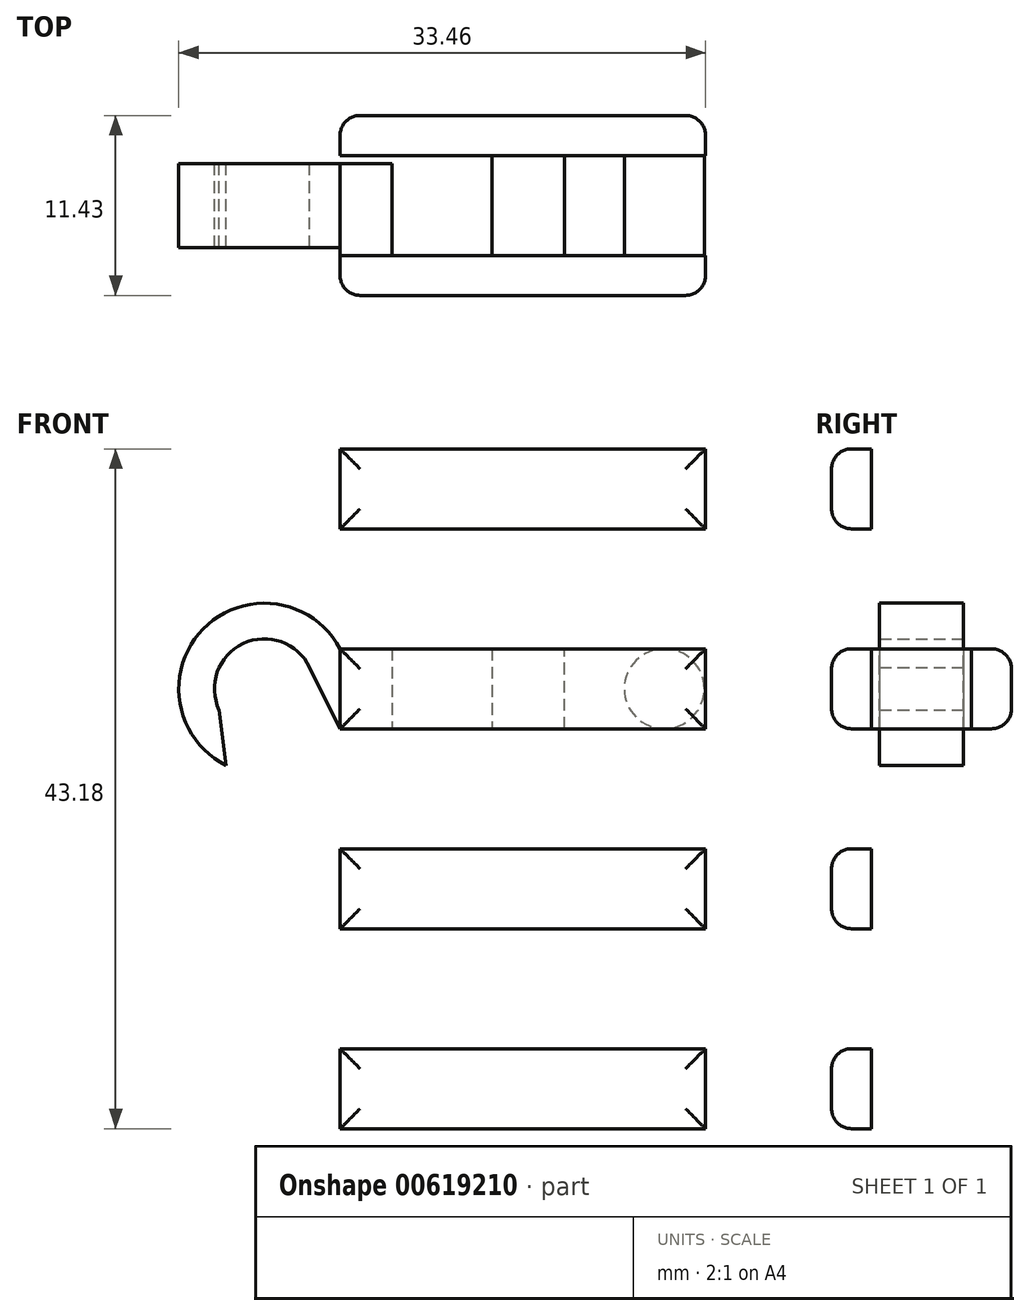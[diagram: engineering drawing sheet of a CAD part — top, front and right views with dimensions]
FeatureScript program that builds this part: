
annotation { "Feature Type Name" : "Feature", "Feature Type Description" : "" }
export const myFeature = defineFeature(function(context is Context, id is Id, definition is map)
    precondition{}
    {
        {
            var Q0;
            Q0=qCreatedBy(makeId("Front.planeOp"),FACE);
            var sketch = newSketch(context, id + "F0", { "sketchPlane" : qUnion([Q0])});
            skLineSegment(sketch, "E0.bottom", {"start": v(0, 0) * mm, "end": v(12.7, 0) * mm});
            skLineSegment(sketch, "E0.top", {"start": v(0, 5.08) * mm, "end": v(12.7, 5.08) * mm});
            skLineSegment(sketch, "E0.right", {"start": v(12.7, 0) * mm, "end": v(12.7, 5.08) * mm});
            skPoint(sketch, "E1.endSnap0", {"position": v(12.7, 2.54) * mm});
            skCircle(sketch, "E2", {"center": v(19.05, 2.54) * mm, "radius": 2.54 * mm});
            skPoint(sketch, "E3.endSnap0", {"position": v(0, 2.54) * mm});
            skArc(sketch, "E4", {"start": v(-3.48, 3.9) * mm, "mid": v(-7.71, 5.4) * mm, "end": v(-9.22, 1.18) * mm});
            skLineSegment(sketch, "E5", {"start": v(0, 5.08) * mm, "end": v(-1.54, 5.08) * mm});
            skLineSegment(sketch, "E6", {"start": v(-1.54, 0) * mm, "end": v(0, 0) * mm});
            skPoint(sketch, "E7.orphan", {"position": v(-3.18, 2.54) * mm});
            skLineSegment(sketch, "E8", {"start": v(-1.54, 0) * mm, "end": v(-3.48, 3.9) * mm});
            skLineSegment(sketch, "E9", {"start": v(-9.22, 1.18) * mm, "end": v(-8.78, -2.32) * mm});
            skLineSegment(sketch, "E10.trimOffspring", {"start": v(-2.8, 2.54) * mm, "end": v(-2.85, 2.54) * mm});
            skArc(sketch, "E11.trimOffspring", {"start": v(-1.54, 5.08) * mm, "mid": v(-10.24, 6.34) * mm, "end": v(-8.78, -2.32) * mm});
            skPoint(sketch, "E3.start.orphan", {"position": v(0, 2.54) * mm});
            skSolve(sketch);
        }
        {
            var Q0;
            Q0 = qSketchRegion(id + "F0", true);
            extrude(context, id + "F1", {"entities" : qUnion([Q0]), "depth" : 6.35 * mm, "offsetDistance" : 25.4 * mm});
        }
        {
            var Q0;
            Q0=makeQuery(id+"F1.opExtrude","CAP_FACE",FACE,{"disambiguationData":[OSD([sQuery(id+"F0.wireOp",EDGE,"E0.bottom"),sQuery(id+"F0.wireOp",EDGE,"E0.top"),sQuery(id+"F0.wireOp",EDGE,"E0.right"),sQuery(id+"F0.wireOp",EDGE,"E4"),sQuery(id+"F0.wireOp",EDGE,"E5"),sQuery(id+"F0.wireOp",EDGE,"E6"),sQuery(id+"F0.wireOp",EDGE,"E8"),sQuery(id+"F0.wireOp",EDGE,"E9"),sQuery(id+"F0.wireOp",EDGE,"E11.trimOffspring")])],"isStart":false});
            var sketch = newSketch(context, id + "F2", { "sketchPlane" : qUnion([Q0])});
            skLineSegment(sketch, "E12.right", {"start": v(21.67, 5.08) * mm, "end": v(21.67, 0) * mm});
            skLineSegment(sketch, "E13.left", {"start": v(21.67, 0) * mm, "end": v(21.67, 5.08) * mm});
            skLineSegment(sketch, "E14.trimOffspring", {"start": v(10.28, 0) * mm, "end": v(12.7, 0) * mm});
            skLineSegment(sketch, "E15.right", {"start": v(-1.54, 5.08) * mm, "end": v(-1.54, 0) * mm});
            skPoint(sketch, "E16.top.end.orphan", {"position": v(2.54, 0) * mm});
            skLineSegment(sketch, "E17", {"start": v(12.7, 0) * mm, "end": v(21.67, 0) * mm});
            skLineSegment(sketch, "E18", {"start": v(21.67, 5.08) * mm, "end": v(-1.54, 5.08) * mm});
            skLineSegment(sketch, "E19", {"start": v(-1.54, 0) * mm, "end": v(21.67, 0) * mm});
            skSolve(sketch);
        }
        {
            var Q0;
            Q0 = qSketchRegion(id + "F2", true);
            extrude(context, id + "F3", {"entities" : qUnion([Q0]), "depth" : 2.54 * mm, "offsetDistance" : 25.4 * mm});
        }
        {
            var Q0;
            Q0=makeQuery(id+"F3.opExtrude","CAP_EDGE",EDGE,{"disambiguationData":[OSD([sQuery(id+"F2.wireOp",EDGE,"E15.right")])],"isStart":false});
            var Q1;
            Q1=makeQuery(id+"F3.opExtrude","CAP_EDGE",EDGE,{"disambiguationData":[OSD([sQuery(id+"F2.wireOp",EDGE,"E18")])],"isStart":false});
            var Q2;
            Q2=makeQuery(id+"F3.opExtrude","CAP_EDGE",EDGE,{"disambiguationData":[OSD([sQuery(id+"F2.wireOp",EDGE,"E13.left")])],"isStart":false});
            var Q3;
            Q3=makeQuery(id+"F3.opExtrude","CAP_FACE",FACE,{"disambiguationData":[OSD([sQuery(id+"F2.wireOp",EDGE,"E13.left"),sQuery(id+"F2.wireOp",EDGE,"E15.right"),sQuery(id+"F2.wireOp",EDGE,"E18"),sQuery(id+"F2.wireOp",EDGE,"E19")])],"isStart":false});
            fillet(context, id + "F4", {"entities" : qUnion([Q0, Q1, Q2, Q3]), "radius" : 1.27 * mm, "tangentPropagation" : true, "allowEdgeOverflow" : false});
        }
        {
            var Q0;
            Q0=qCreatedBy(makeId("Front.planeOp"),FACE);
            cPlane(context, id + "F5", {"entities" : qUnion([Q0]), "cplaneType" : CPlaneType.OFFSET, "offset" : 3.17 * mm, "width" : 152.4 * mm, "height" : 152.4 * mm});
        }
        {
            var Q0;
            Q0=makeQuery(id+"F3.opExtrude","SWEPT_BODY",BODY,{"disambiguationData":[OSD([sQuery(id+"F2.wireOp",EDGE,"E13.left"),sQuery(id+"F2.wireOp",EDGE,"E15.right"),sQuery(id+"F2.wireOp",EDGE,"E18"),sQuery(id+"F2.wireOp",EDGE,"E19")])]});
            var Q1;
            Q1=qCreatedBy(id+"F5.planeOp",FACE);
            mirror(context, id + "F6", {"entities" : qUnion([Q0]), "mirrorPlane" : qUnion([Q1])});
        }
        {
            var Q0;
            Q0=makeQuery(id+"F3.opExtrude","SWEPT_FACE",FACE,{"disambiguationData":[OSD([sQuery(id+"F2.wireOp",EDGE,"E19")])]});
            var sketch = newSketch(context, id + "F7", { "sketchPlane" : qUnion([Q0])});
            skLineSegment(sketch, "E20.bottom", {"start": v(8.1, 0) * mm, "end": v(1.75, 0) * mm});
            skLineSegment(sketch, "E20.top", {"start": v(8.1, 6.35) * mm, "end": v(1.75, 6.35) * mm});
            skLineSegment(sketch, "E20.left", {"start": v(8.1, 0) * mm, "end": v(8.1, 6.35) * mm});
            skLineSegment(sketch, "E20.right", {"start": v(1.75, 0) * mm, "end": v(1.75, 6.35) * mm});
            skPoint(sketch, "E20.middle", {"position": v(4.93, 3.18) * mm});
            skSolve(sketch);
        }
        {
            var Q0;
            {var subQ0=sQuery(id+"F7.wireOp",EDGE,"E20.bottom");Q0=makeQuery(id+"F7.imprint","IMPRINT",FACE,{"disambiguationData":[TD([[makeQuery(id+"F7.imprint","IMPRINT",EDGE,{"derivedFrom":subQ0}),-1.0]])]});}
            extrude(context, id + "F8", {"entities" : qUnion([Q0]), "operationType" : NewBodyOperationType.REMOVE, "oppositeDirection" : true, "depth" : 25.4 * mm, "offsetDistance" : 25.4 * mm});
        }
        {
            var Q0;
            Q0=makeQuery(id+"F2.imprint","IMPRINT",FACE,{"disambiguationData":[TD([[makeQuery(id+"F2.imprint","IMPRINT",EDGE,{"derivedFrom":sQuery(id+"F2.wireOp",EDGE,"E15.right")}),-1.0]])]});
            extrude(context, id + "F9", {"entities" : qUnion([Q0]), "operationType" : NewBodyOperationType.REMOVE, "oppositeDirection" : true, "depth" : 0.5 * mm, "offsetDistance" : 25.4 * mm});
        }
        {
            var Q0;
            {var subQ0=sQuery(id+"F0.wireOp",EDGE,"E8");var subQ1=sQuery(id+"F0.wireOp",EDGE,"E4");var subQ2=sQuery(id+"F0.wireOp",EDGE,"E5");var subQ3=sQuery(id+"F0.wireOp",EDGE,"E0.top");var subQ4=sQuery(id+"F0.wireOp",EDGE,"E6");var subQ5=sQuery(id+"F0.wireOp",EDGE,"E0.bottom");var subQ6=sQuery(id+"F0.wireOp",EDGE,"E9");var subQ7=sQuery(id+"F0.wireOp",EDGE,"E11.trimOffspring");Q0=makeQuery(id+"F8.boolean.opBoolean","SPLIT",FACE,{"disambiguationData":[TD([makeQuery(id+"F1.opExtrude","SWEPT_FACE",FACE,{"disambiguationData":[OSD([subQ1])]})])],"derivedFrom":makeQuery(id+"F1.opExtrude","CAP_FACE",FACE,{"disambiguationData":[OSD([subQ5,subQ3,sQuery(id+"F0.wireOp",EDGE,"E0.right"),subQ1,subQ2,subQ4,subQ0,subQ6,subQ7])],"isStart":true})});}
            extrude(context, id + "F10", {"entities" : qUnion([Q0]), "operationType" : NewBodyOperationType.REMOVE, "oppositeDirection" : true, "depth" : 0.5 * mm, "offsetDistance" : 25.4 * mm});
        }
        {
            var Q0;
            Q0=makeQuery(id+"F3.opExtrude","SWEPT_BODY",BODY,{"disambiguationData":[OSD([sQuery(id+"F2.wireOp",EDGE,"E13.left"),sQuery(id+"F2.wireOp",EDGE,"E15.right"),sQuery(id+"F2.wireOp",EDGE,"E18"),sQuery(id+"F2.wireOp",EDGE,"E19")])]});
            transform(context, id + "F11", {"entities" : qUnion([Q0]), "transformType" : TransformType.TRANSLATION_3D, "dx" : 0 * mm, "dy" : 0 * mm, "dz" : 12.7 * mm, "makeCopy" : true});
        }
        {
            var Q0;
            Q0=makeQuery(id+"F11.opPattern","COPY",BODY,{"derivedFrom":makeQuery(id+"F3.opExtrude","SWEPT_BODY",BODY,{"disambiguationData":[OSD([sQuery(id+"F2.wireOp",EDGE,"E13.left"),sQuery(id+"F2.wireOp",EDGE,"E15.right"),sQuery(id+"F2.wireOp",EDGE,"E18"),sQuery(id+"F2.wireOp",EDGE,"E19")])]}),"instanceName":"1"});
            var Q1;
            Q1=makeQuery(id+"F3.opExtrude","SWEPT_BODY",BODY,{"disambiguationData":[OSD([sQuery(id+"F2.wireOp",EDGE,"E13.left"),sQuery(id+"F2.wireOp",EDGE,"E15.right"),sQuery(id+"F2.wireOp",EDGE,"E18"),sQuery(id+"F2.wireOp",EDGE,"E19")])]});
            transform(context, id + "F12", {"entities" : qUnion([Q0, Q1]), "transformType" : TransformType.TRANSLATION_3D, "dx" : 0 * mm, "dy" : 0 * mm, "dz" : -25.4 * mm, "makeCopy" : true});
        }
    });
